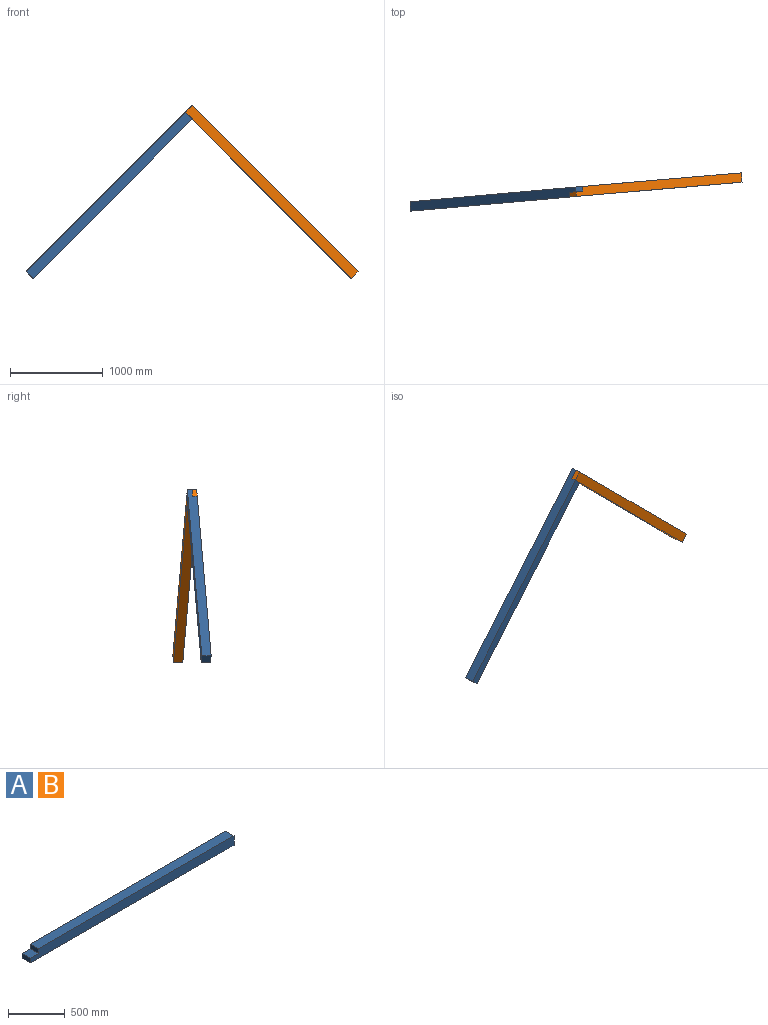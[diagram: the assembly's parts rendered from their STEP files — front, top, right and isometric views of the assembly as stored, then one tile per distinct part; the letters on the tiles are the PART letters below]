
ASSEMBLY  parts=2 mates=1
PART A: 8 faces, bbox 2540x101.6x101.6 mm
  f0: plane 101.6x50.8mm, normal (-1,0,0), area 5161.3mm2, adj f1,f5,f6,f7
  f1: plane 101.6x101.6mm, normal (0,0,1), area 10322.6mm2, adj f0,f2,f6,f7
  f2: plane 101.6x50.8mm, normal (-1,0,0), area 5161.3mm2, adj f1,f3,f6,f7
  f3: plane 2540x101.6mm, normal (0,0,-1), area 258064mm2, adj f2,f4,f6,f7
  f4: plane 101.6x101.6mm, normal (1,0,0), area 10322.6mm2, adj f3,f5,f6,f7
  f5: plane 2438.4x101.6mm, normal (0,0,1), area 247741.4mm2, adj f0,f4,f6,f7
  f6: plane 2540x101.6mm, normal (0,-1,0), area 252902.7mm2, adj f0,f1,f2,f3,f4,f5
  f7: plane 2540x101.6mm, normal (0,1,0), area 252902.7mm2, adj f0,f1,f2,f3,f4,f5
PART B: same geometry as A
PLACE A rot(axis=(0.25,0.7,-0.67),145.2deg) t=(616.36,269.02,810.48)mm
PLACE B rot(axis=(-0.87,0.32,0.39),100.3deg) t=(1197.58,217.89,810.48)mm
MATE fastened A.f1 <-> B.f1  axis (0.09,-1,0) through (906.97,243.46,1169.6)mm
